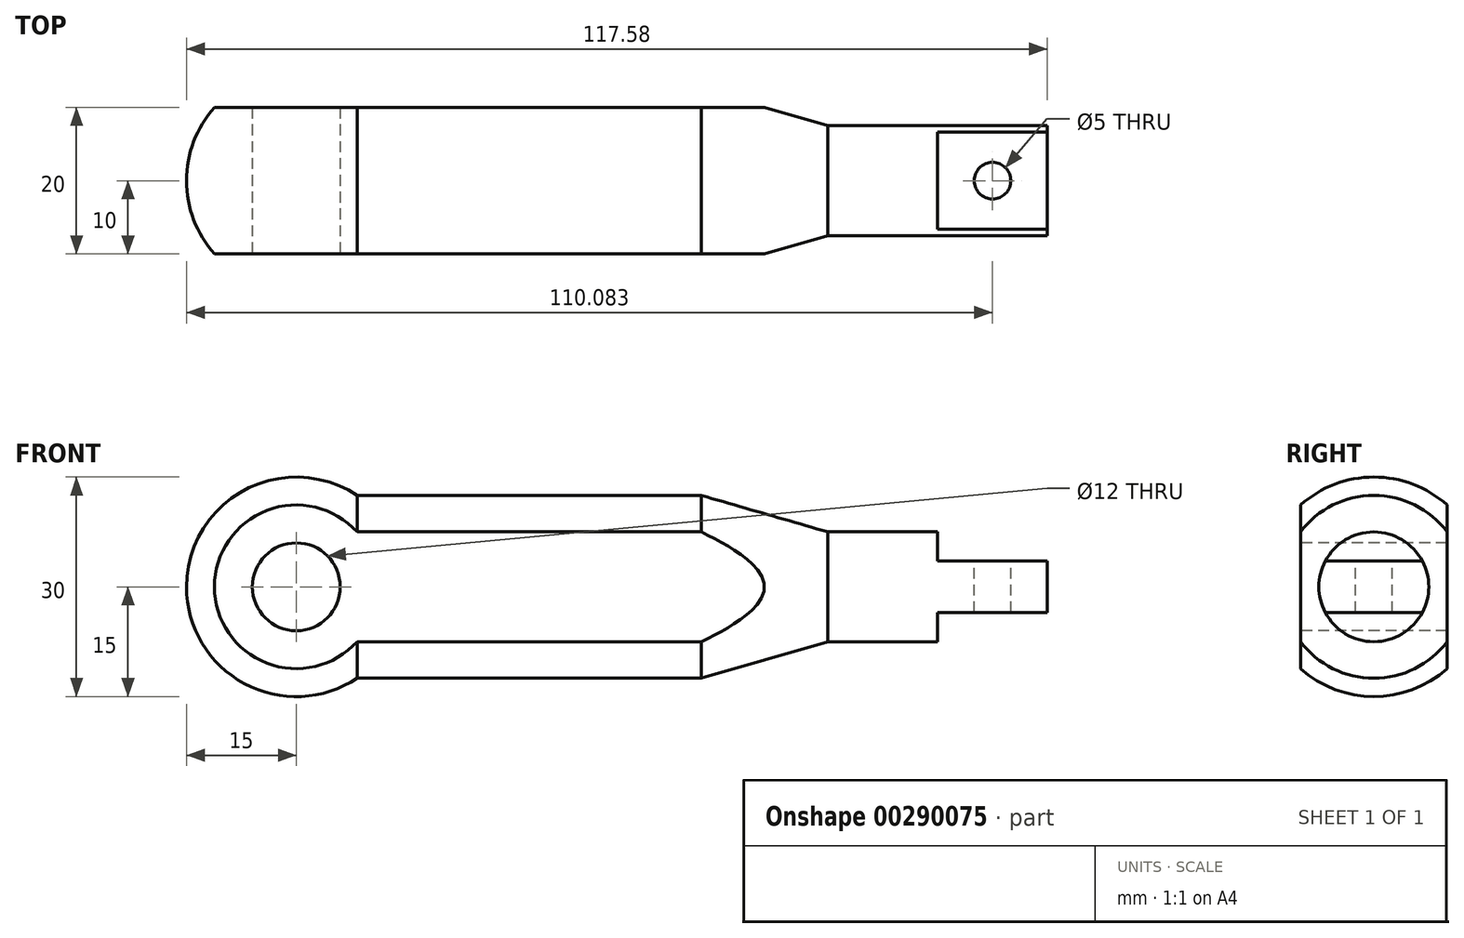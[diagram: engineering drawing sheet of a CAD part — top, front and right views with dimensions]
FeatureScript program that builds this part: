
annotation { "Feature Type Name" : "Feature", "Feature Type Description" : "" }
export const myFeature = defineFeature(function(context is Context, id is Id, definition is map)
    precondition{}
    {
        {
            var Q0;
            Q0=qCreatedBy(makeId("Front.planeOp"),FACE);
            var sketch = newSketch(context, id + "F0", { "sketchPlane" : qUnion([Q0])});
            skLineSegment(sketch, "E0", {"start": v(0, 0) * mm, "end": v(129.64, 0) * mm, "construction": true});
            skArc(sketch, "E1", {"start": v(-15, 0) * mm, "mid": v(-7.1, 13.22) * mm, "end": v(8.3, 12.5) * mm});
            skLineSegment(sketch, "E2", {"start": v(8.3, 12.5) * mm, "end": v(55.3, 12.5) * mm});
            skLineSegment(sketch, "E3", {"start": v(55.3, 12.5) * mm, "end": v(72.58, 7.5) * mm});
            skLineSegment(sketch, "E4", {"start": v(72.58, 7.5) * mm, "end": v(102.58, 7.5) * mm});
            skLineSegment(sketch, "E5", {"start": v(102.58, 7.5) * mm, "end": v(102.58, 0) * mm});
            skLineSegment(sketch, "E6", {"start": v(102.58, 0) * mm, "end": v(-15, 0) * mm});
            skSolve(sketch);
        }
        {
            var Q0;
            Q0 = qSketchRegion(id + "F0", true);
            var Q1;
            Q1=sQuery(id+"F0.wireOp",EDGE,"E0");
            revolve(context, id + "F1", {"entities" : qUnion([Q0]), "axis" : qUnion([Q1]), "revolveType" : RevolveType.FULL});
        }
        {
            var Q0;
            Q0=qCreatedBy(makeId("Front.planeOp"),FACE);
            var sketch = newSketch(context, id + "F2", { "sketchPlane" : qUnion([Q0])});
            skLineSegment(sketch, "E7.bottom", {"start": v(102.58, 7.5) * mm, "end": v(87.58, 7.5) * mm});
            skLineSegment(sketch, "E7.top", {"start": v(102.58, 3.5) * mm, "end": v(87.58, 3.5) * mm});
            skLineSegment(sketch, "E7.left", {"start": v(102.58, 7.5) * mm, "end": v(102.58, 3.5) * mm});
            skLineSegment(sketch, "E7.right", {"start": v(87.58, 7.5) * mm, "end": v(87.58, 3.5) * mm});
            skLineSegment(sketch, "E8", {"start": v(87.58, 7.5) * mm, "end": v(102.58, 7.5) * mm});
            skLineSegment(sketch, "E9", {"start": v(74.7, 0) * mm, "end": v(112.57, 0) * mm, "construction": true});
            skLineSegment(sketch, "E10.MirrorCS", {"start": v(102.58, -7.5) * mm, "end": v(87.58, -7.5) * mm});
            skLineSegment(sketch, "E11.MirrorCS", {"start": v(87.58, -7.5) * mm, "end": v(102.58, -7.5) * mm});
            skLineSegment(sketch, "E12.MirrorCS", {"start": v(87.58, -7.5) * mm, "end": v(87.58, -3.5) * mm});
            skLineSegment(sketch, "E13.MirrorCS", {"start": v(102.58, -7.5) * mm, "end": v(102.58, -3.5) * mm});
            skLineSegment(sketch, "E14.MirrorCS", {"start": v(102.58, -3.5) * mm, "end": v(87.58, -3.5) * mm});
            skSolve(sketch);
        }
        {
            var Q0;
            Q0 = qSketchRegion(id + "F2", true);
            extrude(context, id + "F3", {"entities" : qUnion([Q0]), "operationType" : NewBodyOperationType.REMOVE, "endBound" : BoundingType.THROUGH_ALL, "oppositeDirection" : true, "depth" : 25 * mm, "hasSecondDirection" : true, "secondDirectionBound" : SecondDirectionBoundingType.THROUGH_ALL, "secondDirectionOppositeDirection" : false, "secondDirectionDepth" : 25 * mm});
        }
        {
            var Q0;
            Q0=makeQuery(id+"F1.opRevolve","SWEPT_FACE",FACE,{"disambiguationData":[OSD([sQuery(id+"F0.wireOp",EDGE,"E5")])]});
            var sketch = newSketch(context, id + "F4", { "sketchPlane" : qUnion([Q0])});
            skLineSegment(sketch, "E15", {"start": v(-10, 11.18) * mm, "end": v(-10, -11.18) * mm});
            skLineSegment(sketch, "E16", {"start": v(10, 11.18) * mm, "end": v(10, -11.18) * mm});
            skArc(sketch, "E17", {"start": v(-10, 11.18) * mm, "mid": v(-15, 0) * mm, "end": v(-10, -11.18) * mm});
            skLineSegment(sketch, "E18", {"start": v(0, 0) * mm, "end": v(0, 30.58) * mm, "construction": true});
            skArc(sketch, "E19.trimOffspring", {"start": v(10, -11.18) * mm, "mid": v(15, 0) * mm, "end": v(10, 11.18) * mm});
            skSolve(sketch);
        }
        {
            var Q0;
            Q0 = qSketchRegion(id + "F4", true);
            extrude(context, id + "F5", {"entities" : qUnion([Q0]), "operationType" : NewBodyOperationType.REMOVE, "endBound" : BoundingType.THROUGH_ALL, "oppositeDirection" : true, "depth" : 25 * mm});
        }
        {
            var Q0;
            Q0=makeQuery(id+"F5.boolean.opBoolean","COPY",FACE,{"derivedFrom":makeQuery(id+"F5.opExtrude","SWEPT_FACE",FACE,{"disambiguationData":[OSD([sQuery(id+"F4.wireOp",EDGE,"E15")])]})});
            var sketch = newSketch(context, id + "F6", { "sketchPlane" : qUnion([Q0])});
            skCircle(sketch, "E20", {"center": v(0, 0) * mm, "radius": 6 * mm});
            skSolve(sketch);
        }
        {
            var Q0;
            Q0=makeQuery(id+"F6.imprint","IMPRINT",FACE,{"disambiguationData":[TD([[makeQuery(id+"F6.imprint","IMPRINT",EDGE,{"derivedFrom":sQuery(id+"F6.wireOp",EDGE,"E20")}),1.0]])]});
            extrude(context, id + "F7", {"entities" : qUnion([Q0]), "operationType" : NewBodyOperationType.REMOVE, "endBound" : BoundingType.THROUGH_ALL, "oppositeDirection" : true, "depth" : 25 * mm});
        }
        {
            var Q0;
            Q0=makeQuery(id+"F3.boolean.opBoolean","COPY",FACE,{"derivedFrom":makeQuery(id+"F3.opExtrude","SWEPT_FACE",FACE,{"disambiguationData":[OSD([sQuery(id+"F2.wireOp",EDGE,"E7.top")])]})});
            var sketch = newSketch(context, id + "F8", { "sketchPlane" : qUnion([Q0])});
            skCircle(sketch, "E21", {"center": v(95.08, 0) * mm, "radius": 2.5 * mm});
            skSolve(sketch);
        }
        {
            var Q0;
            Q0 = qSketchRegion(id + "F8", true);
            extrude(context, id + "F9", {"entities" : qUnion([Q0]), "operationType" : NewBodyOperationType.REMOVE, "endBound" : BoundingType.THROUGH_ALL, "oppositeDirection" : true, "depth" : 25 * mm});
        }
    });
